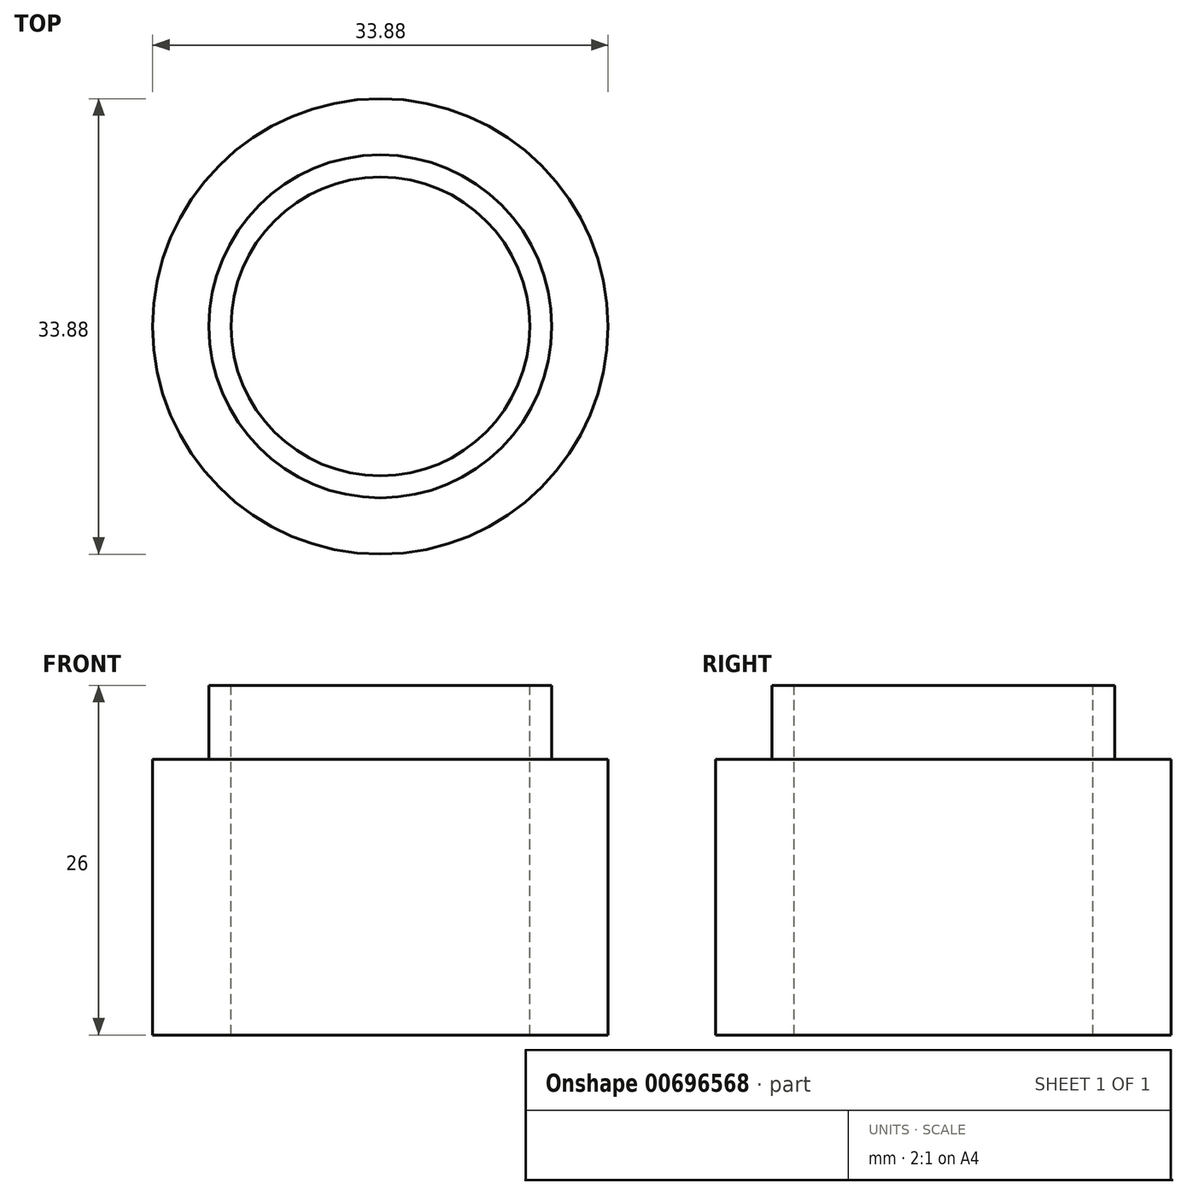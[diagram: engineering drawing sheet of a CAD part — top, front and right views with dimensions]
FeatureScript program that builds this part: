
annotation { "Feature Type Name" : "Feature", "Feature Type Description" : "" }
export const myFeature = defineFeature(function(context is Context, id is Id, definition is map)
    precondition{}
    {
        {
            var Q0;
            Q0=qCreatedBy(makeId("Top.planeOp"),FACE);
            var sketch = newSketch(context, id + "F0", { "sketchPlane" : qUnion([Q0])});
            skCircle(sketch, "E0", {"center": v(0, 0) * mm, "radius": 16.93 * mm});
            skSolve(sketch);
        }
        {
            var Q0;
            Q0 = qSketchRegion(id + "F0", true);
            extrude(context, id + "F1", {"entities" : qUnion([Q0]), "depth" : 20.5 * mm, "offsetDistance" : 25.4 * mm});
        }
        {
            var Q0;
            Q0=makeQuery(id+"F1.opExtrude","CAP_FACE",FACE,{"disambiguationData":[OSD([sQuery(id+"F0.wireOp",EDGE,"E0")])],"isStart":false});
            var sketch = newSketch(context, id + "F2", { "sketchPlane" : qUnion([Q0])});
            skCircle(sketch, "E1", {"center": v(0, 0) * mm, "radius": 12.75 * mm});
            skSolve(sketch);
        }
        {
            var Q0;
            Q0 = qSketchRegion(id + "F2", true);
            extrude(context, id + "F3", {"entities" : qUnion([Q0]), "operationType" : NewBodyOperationType.ADD, "depth" : 26 * mm - 20.5 * mm, "offsetDistance" : 25.4 * mm});
        }
        {
            var Q0;
            Q0=makeQuery(id+"F3.opExtrude","CAP_FACE",FACE,{"disambiguationData":[OSD([sQuery(id+"F2.wireOp",EDGE,"E1")])],"isStart":false});
            var sketch = newSketch(context, id + "F4", { "sketchPlane" : qUnion([Q0])});
            skCircle(sketch, "E2", {"center": v(0, 0) * mm, "radius": 11.11 * mm});
            skSolve(sketch);
        }
        {
            var Q0;
            Q0 = qSketchRegion(id + "F4", true);
            extrude(context, id + "F5", {"entities" : qUnion([Q0]), "operationType" : NewBodyOperationType.REMOVE, "oppositeDirection" : true, "depth" : 40.13 * mm, "offsetDistance" : 25.4 * mm});
        }
    });
